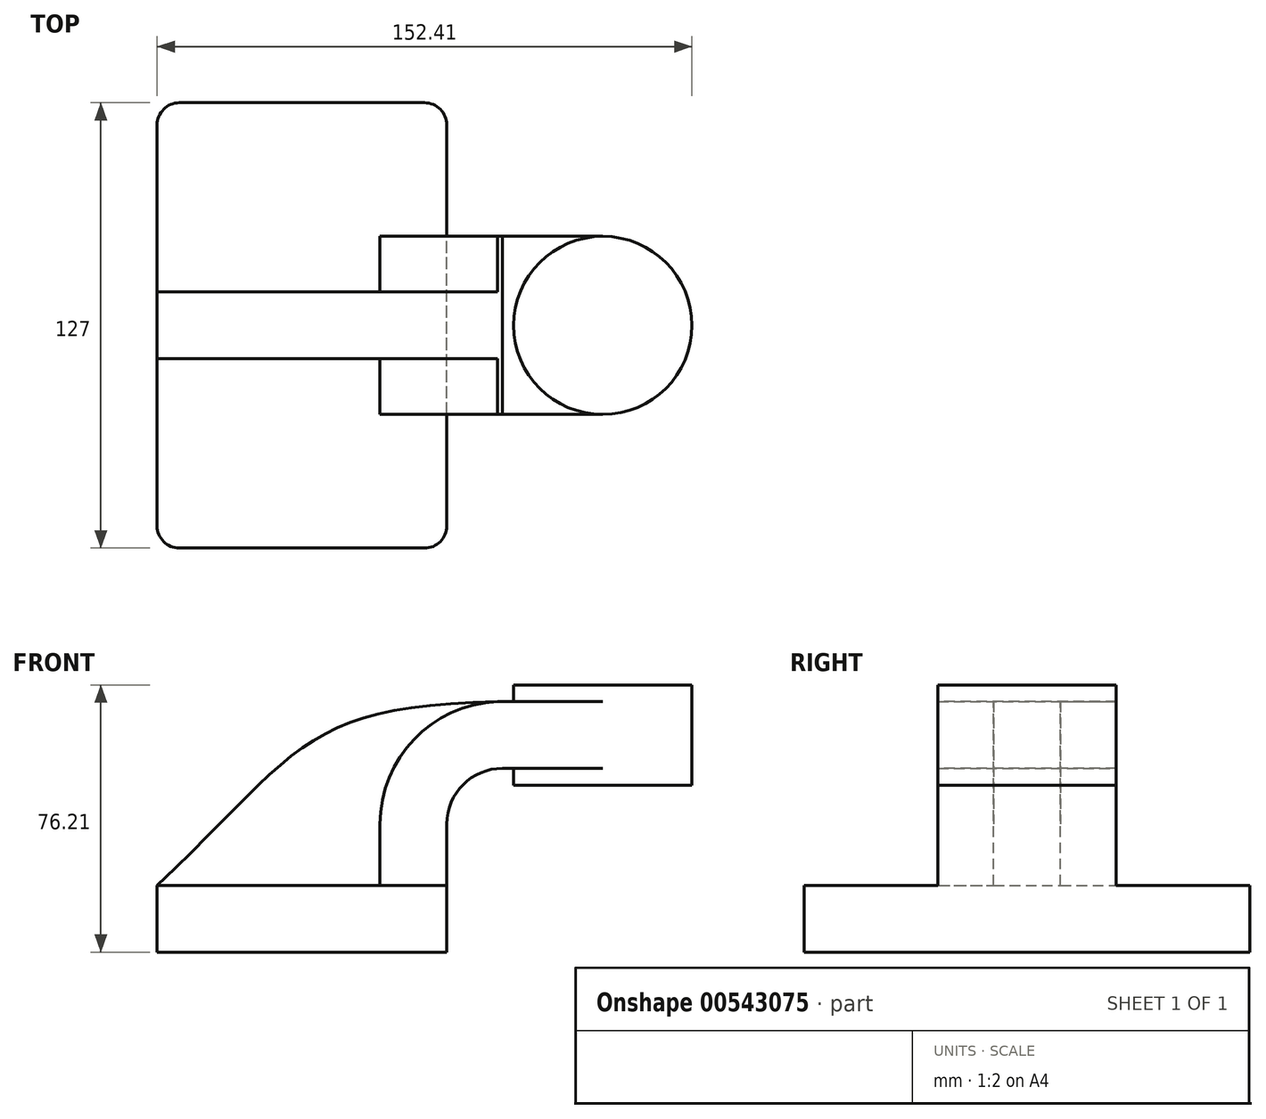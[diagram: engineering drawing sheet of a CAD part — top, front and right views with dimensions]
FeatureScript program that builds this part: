
annotation { "Feature Type Name" : "Feature", "Feature Type Description" : "" }
export const myFeature = defineFeature(function(context is Context, id is Id, definition is map)
    precondition{}
    {
        {
            var Q0;
            Q0=qCreatedBy(makeId("Front.planeOp"),FACE);
            var sketch = newSketch(context, id + "F0", { "sketchPlane" : qUnion([Q0])});
            skLineSegment(sketch, "E0.bottom", {"start": v(-41.28, 9.52) * mm, "end": v(41.28, 9.53) * mm});
            skLineSegment(sketch, "E0.top", {"start": v(-41.28, -9.52) * mm, "end": v(41.28, -9.52) * mm});
            skLineSegment(sketch, "E0.left", {"start": v(-41.28, 9.52) * mm, "end": v(-41.27, -9.53) * mm});
            skLineSegment(sketch, "E0.right", {"start": v(41.28, 9.53) * mm, "end": v(41.28, -9.52) * mm});
            skPoint(sketch, "E0.middle", {"position": v(0, 0) * mm});
            skLineSegment(sketch, "E1.bottom", {"start": v(111.12, 38.1) * mm, "end": v(60.33, 38.1) * mm});
            skLineSegment(sketch, "E1.top", {"start": v(111.12, 66.67) * mm, "end": v(60.33, 66.67) * mm});
            skLineSegment(sketch, "E1.left", {"start": v(111.12, 38.1) * mm, "end": v(111.12, 66.67) * mm});
            skLineSegment(sketch, "E1.right", {"start": v(60.33, 38.1) * mm, "end": v(60.33, 66.67) * mm});
            skPoint(sketch, "E1.middle", {"position": v(85.72, 52.39) * mm});
            skLineSegment(sketch, "E2", {"start": v(41.27, 9.53) * mm, "end": v(41.27, 27) * mm});
            skArc(sketch, "E3", {"start": v(41.27, 27) * mm, "mid": v(45.92, 38.23) * mm, "end": v(57.15, 42.88) * mm});
            skLineSegment(sketch, "E4", {"start": v(57.15, 42.88) * mm, "end": v(85.73, 42.88) * mm});
            skLineSegment(sketch, "E5.0", {"start": v(57.15, 61.93) * mm, "end": v(85.73, 61.93) * mm});
            skArc(sketch, "E5.1", {"start": v(22.22, 27) * mm, "mid": v(32.45, 51.7) * mm, "end": v(57.15, 61.93) * mm});
            skLineSegment(sketch, "E5.2", {"start": v(22.22, 9.53) * mm, "end": v(22.22, 27) * mm});
            skFitSpline(sketch, "E6", {"points": [v(-41.28, 9.52) * mm, v(57.15, 61.93) * mm], "startDerivative": vector(123.83, 117.34) * mm, "endDerivative": vector(171.45, 3.28) * mm});
            skLineSegment(sketch, "E7", {"start": v(85.72, 66.67) * mm, "end": v(85.72, 38.1) * mm});
            skSolve(sketch);
        }
        {
            var Q0;
            Q0=makeQuery(id+"F0.imprint","IMPRINT",FACE,{"disambiguationData":[TD([[makeQuery(id+"F0.imprint","IMPRINT",EDGE,{"derivedFrom":sQuery(id+"F0.wireOp",EDGE,"E0.top")}),1.0]])]});
            extrude(context, id + "F1", {"entities" : qUnion([Q0]), "endBound" : BoundingType.SYMMETRIC, "depth" : 127 * mm, "offsetDistance" : 25.4 * mm});
        }
        {
            var Q0;
            {var subQ1=sQuery(id+"F0.wireOp",EDGE,"E2");Q0=makeQuery(id+"F0.imprint","IMPRINT",FACE,{"disambiguationData":[TD([[makeQuery(id+"F0.imprint","IMPRINT",EDGE,{"derivedFrom":subQ1}),1.0]])]});}
            var Q1;
            {var subQ5=sQuery(id+"F0.wireOp",EDGE,"brmncPR0-1tl2-Qqjq-xkQZ-Rsg0DdkdDkko");Q1=makeQuery(id+"F0.imprint","IMPRINT",FACE,{"disambiguationData":[TD([[makeQuery(id+"F0.imprint","IMPRINT",EDGE,{"derivedFrom":subQ5}),-1.0]])]});}
            extrude(context, id + "F2", {"entities" : qUnion([Q0, Q1]), "operationType" : NewBodyOperationType.ADD, "endBound" : BoundingType.SYMMETRIC, "depth" : 50.8 * mm, "offsetDistance" : 25.4 * mm});
        }
        {
            var Q0;
            {var subQ3=sQuery(id+"F0.wireOp",EDGE,"E5.2");Q0=makeQuery(id+"F0.imprint","IMPRINT",FACE,{"disambiguationData":[TD([[makeQuery(id+"F0.imprint","IMPRINT",EDGE,{"derivedFrom":subQ3}),1.0]])]});}
            extrude(context, id + "F3", {"entities" : qUnion([Q0]), "operationType" : NewBodyOperationType.ADD, "endBound" : BoundingType.SYMMETRIC, "depth" : 19.05 * mm, "offsetDistance" : 25.4 * mm});
        }
        {
            var Q0;
            {var subQ0=sQuery(id+"F0.wireOp",EDGE,"E4");var subQ1=sQuery(id+"F0.wireOp",EDGE,"E1.right");var subQ2=makeQuery(id+"F0.imprint","INTERSECT",VERTEX,{"derivedFrom":[subQ1,subQ0]});Q0=makeQuery(id+"F0.imprint","IMPRINT",FACE,{"disambiguationData":[TD([[makeQuery(id+"F0.imprint","IMPRINT",EDGE,{"disambiguationData":[TD([[subQ2,-1.0]])],"derivedFrom":subQ1}),-1.0]])]});}
            extrude(context, id + "F4", {"entities" : qUnion([Q0]), "operationType" : NewBodyOperationType.ADD, "endBound" : BoundingType.SYMMETRIC, "depth" : 50.8 * mm, "offsetDistance" : 25.4 * mm});
        }
        {
            var Q0;
            {var subQ4=sQuery(id+"F0.wireOp",EDGE,"E1.left");Q0=makeQuery(id+"F0.imprint","IMPRINT",FACE,{"disambiguationData":[TD([[makeQuery(id+"F0.imprint","IMPRINT",EDGE,{"derivedFrom":subQ4}),1.0]])]});}
            var Q1;
            Q1=sQuery(id+"F0.wireOp",EDGE,"E7");
            revolve(context, id + "F5", {"operationType" : NewBodyOperationType.ADD, "entities" : qUnion([Q0]), "axis" : qUnion([Q1]), "revolveType" : RevolveType.ONE_DIRECTION, "angle" : 360 * degree});
        }
        {
            var Q0;
            Q0=makeQuery(id+"F1.opExtrude","CAP_EDGE",EDGE,{"disambiguationData":[OSD([sQuery(id+"F0.wireOp",EDGE,"E0.right")])],"isStart":false});
            var Q1;
            Q1=makeQuery(id+"F1.opExtrude","CAP_EDGE",EDGE,{"disambiguationData":[OSD([sQuery(id+"F0.wireOp",EDGE,"E0.left")])],"isStart":false});
            var Q2;
            Q2=makeQuery(id+"F1.opExtrude","CAP_EDGE",EDGE,{"disambiguationData":[OSD([sQuery(id+"F0.wireOp",EDGE,"E0.right")])],"isStart":true});
            var Q3;
            Q3=makeQuery(id+"F1.opExtrude","CAP_EDGE",EDGE,{"disambiguationData":[OSD([sQuery(id+"F0.wireOp",EDGE,"E0.left")])],"isStart":true});
            fillet(context, id + "F6", {"entities" : qUnion([Q0, Q1, Q2, Q3]), "radius" : 6.35 * mm, "tangentPropagation" : true, "allowEdgeOverflow" : false});
        }
    });
